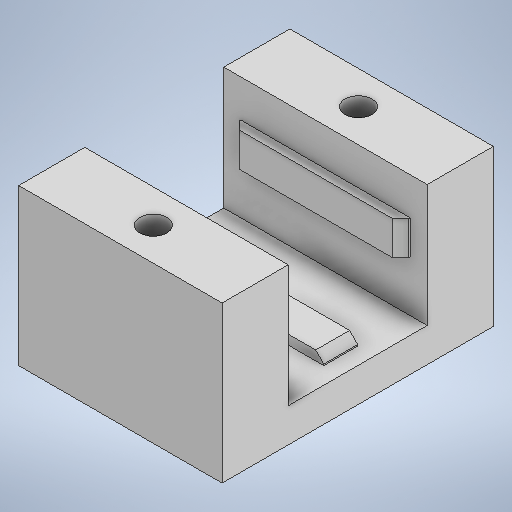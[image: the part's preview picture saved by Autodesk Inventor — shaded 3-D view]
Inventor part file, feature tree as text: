
AUTODESK INVENTOR PART (.ipt)
format: ipt  version: 2025 (Build 290162010, 162A)  size: 277,504 bytes
history: native  units: in
note: dims shown in document units (in); Inventor stores cm internally (conversion verified against a paired STEP export)
features: extrude x6, sketch x6, chamfer x2
ambient origin geometry x8: Origin, YZ Plane, XZ Plane, XY Plane, X Axis, Y Axis, Z Axis, Center Point
bodies: Body1 (feature_tree)
feature tree (14):
  extrude  "Extrusion16"  Depth=1.1811in
  extrude  "Extrusion17"  Depth=0.7087in TaperAngle=0.0deg
  extrude  "Extrusion18"  Depth=0.2953in
  extrude  "Extrusion19"  Depth=0.9843in
  extrude  "Extrusion20"  Depth=0.0551in TaperAngle=0.0deg
  chamfer  "Fasen4"  Distance=0.0551in
  extrude  "Extrusion21"  Depth=0.0551in TaperAngle=0.0deg
  chamfer  "Fasen5"  Distance=0.0787in Angle=45.0deg
  sketch  "Skizze16"  dims[d82=1.5748in d83=1.1811in]
  sketch  "Skizze17"  dims[d84=0.1969in d85=0.0in d89=0.7087in d90=0.0in]
  sketch  "Skizze19"  dims[d91=0.8071in d92=0.2953in]
  sketch  "Skizze20"  dims[d93=0.1969in d94=0.9843in]
  sketch  "Skizze21"  dims[d95=0.5906in d96=0.0551in d97=0.0in d98=0.0551in d99=0.0in]
  sketch  "Skizze22"  dims[d100=0.1969in d101=0.0551in d102=0.0in d103=0.0472in d104=0.0787in d105=45.0deg d106=0.1575in d107=0.1919in d108=0.0in d109=0.0in d110=0.0787in d111=0.0787in d112=45.0deg d37=0.0197in d38=0.0344in d39=0.0197in d40=0.0344in d41=0.0197in d42=0.0344in]
